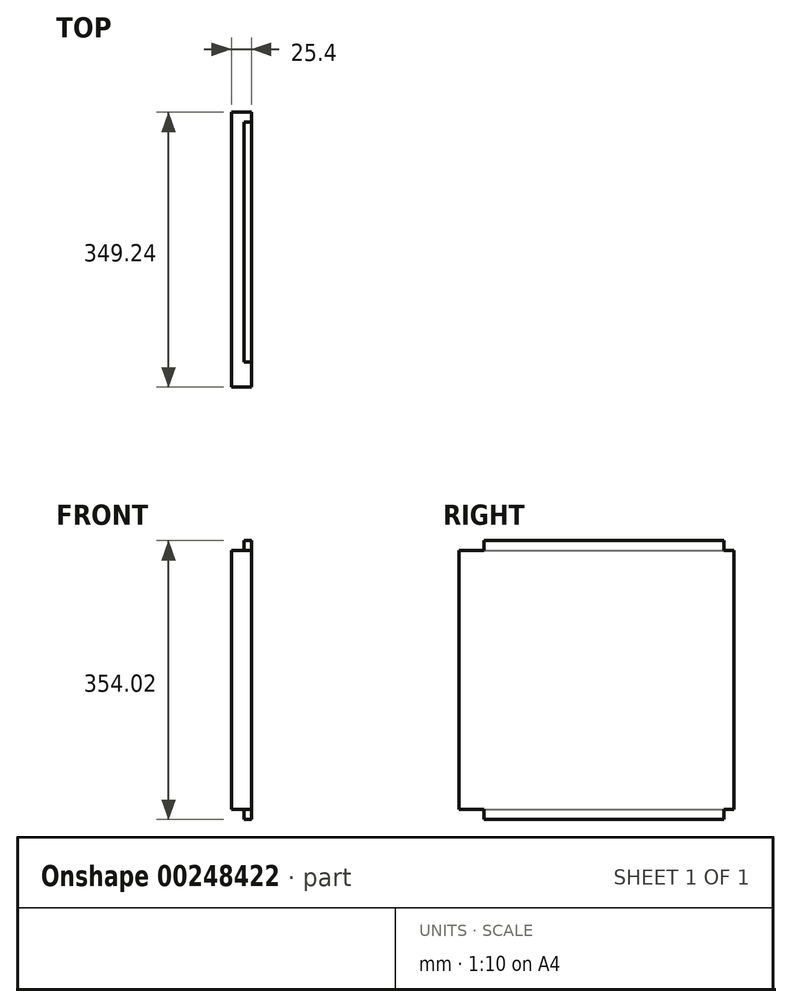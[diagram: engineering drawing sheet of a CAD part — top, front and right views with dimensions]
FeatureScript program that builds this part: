
annotation { "Feature Type Name" : "Feature", "Feature Type Description" : "" }
export const myFeature = defineFeature(function(context is Context, id is Id, definition is map)
    precondition{}
    {
        {
            var Q0;
            Q0=qCreatedBy(makeId("Right.planeOp"),FACE);
            var sketch = newSketch(context, id + "F0", { "sketchPlane" : qUnion([Q0])});
            skLineSegment(sketch, "E0.bottom", {"start": v(-174.62, 164.3) * mm, "end": v(174.63, 164.3) * mm});
            skLineSegment(sketch, "E0.top", {"start": v(-174.63, -164.3) * mm, "end": v(174.62, -164.3) * mm});
            skLineSegment(sketch, "E0.left", {"start": v(-174.62, 164.3) * mm, "end": v(-174.63, -164.3) * mm});
            skLineSegment(sketch, "E0.right", {"start": v(174.63, 164.3) * mm, "end": v(174.62, -164.3) * mm});
            skPoint(sketch, "E0.middle", {"position": v(0, 0) * mm});
            skSolve(sketch);
        }
        {
            var Q0;
            Q0 = qSketchRegion(id + "F0", true);
            extrude(context, id + "F1", {"entities" : qUnion([Q0]), "endBound" : BoundingType.SYMMETRIC, "depth" : 25.4 * mm});
        }
        {
            var Q0;
            Q0=makeQuery(id+"F1.opExtrude","SWEPT_FACE",FACE,{"disambiguationData":[OSD([sQuery(id+"F0.wireOp",EDGE,"E0.bottom")])]});
            var sketch = newSketch(context, id + "F2", { "sketchPlane" : qUnion([Q0])});
            skLineSegment(sketch, "E1", {"start": v(3.18, -142.87) * mm, "end": v(3.18, 161.93) * mm});
            skLineSegment(sketch, "E2", {"start": v(3.18, 161.93) * mm, "end": v(12.7, 161.93) * mm});
            skLineSegment(sketch, "E3", {"start": v(3.18, -142.88) * mm, "end": v(12.7, -142.88) * mm});
            skLineSegment(sketch, "E4", {"start": v(12.7, -142.88) * mm, "end": v(12.7, 161.93) * mm});
            skSolve(sketch);
        }
        {
            var Q0;
            Q0=makeQuery(id+"F2.imprint","IMPRINT",FACE,{"disambiguationData":[TD([[makeQuery(id+"F2.imprint","IMPRINT",EDGE,{"derivedFrom":sQuery(id+"F2.wireOp",EDGE,"E1")}),-1.0]])]});
            extrude(context, id + "F3", {"entities" : qUnion([Q0]), "operationType" : NewBodyOperationType.ADD, "depth" : 12.7 * mm});
        }
        {
            var Q0;
            Q0=makeQuery(id+"F1.opExtrude","SWEPT_FACE",FACE,{"disambiguationData":[OSD([sQuery(id+"F0.wireOp",EDGE,"E0.top")])]});
            var sketch = newSketch(context, id + "F4", { "sketchPlane" : qUnion([Q0])});
            skLineSegment(sketch, "E5", {"start": v(3.17, 142.88) * mm, "end": v(3.18, -161.93) * mm});
            skLineSegment(sketch, "E6", {"start": v(12.7, 142.88) * mm, "end": v(3.17, 142.88) * mm});
            skLineSegment(sketch, "E7", {"start": v(12.7, -161.93) * mm, "end": v(3.18, -161.93) * mm});
            skLineSegment(sketch, "E8", {"start": v(12.7, 142.88) * mm, "end": v(12.7, -161.93) * mm});
            skSolve(sketch);
        }
        {
            var Q0;
            Q0=makeQuery(id+"F4.imprint","IMPRINT",FACE,{"disambiguationData":[TD([[makeQuery(id+"F4.imprint","IMPRINT",EDGE,{"derivedFrom":sQuery(id+"F4.wireOp",EDGE,"E5")}),1.0]])]});
            extrude(context, id + "F5", {"entities" : qUnion([Q0]), "operationType" : NewBodyOperationType.ADD, "depth" : 12.7 * mm});
        }
    });
